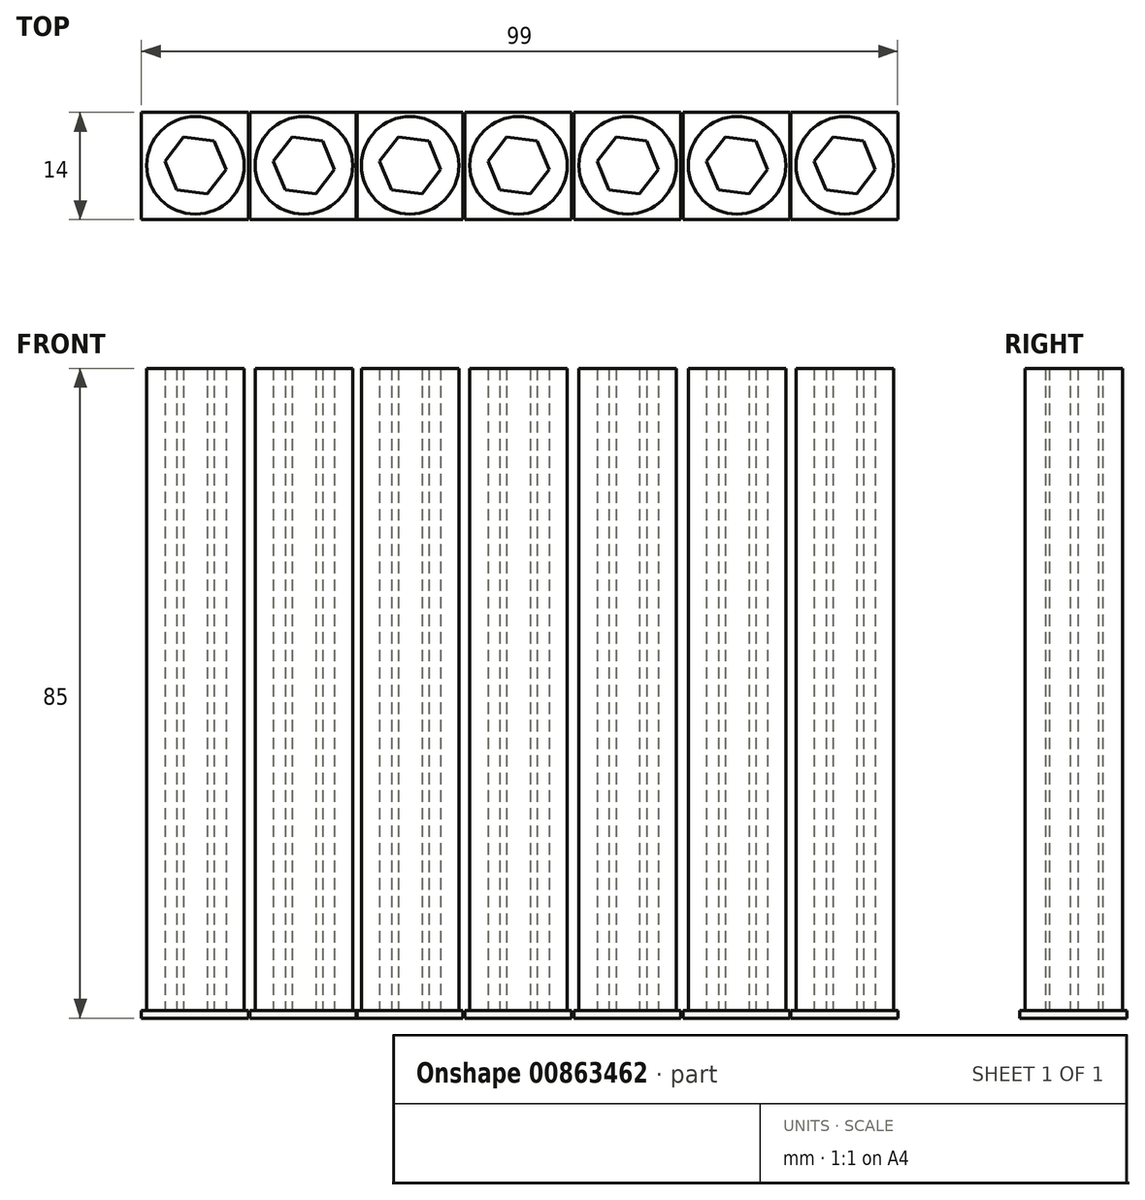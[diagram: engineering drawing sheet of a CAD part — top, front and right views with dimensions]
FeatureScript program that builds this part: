
annotation { "Feature Type Name" : "Feature", "Feature Type Description" : "" }
export const myFeature = defineFeature(function(context is Context, id is Id, definition is map)
    precondition{}
    {
        {
            var Q0;
            Q0=qCreatedBy(makeId("Top.planeOp"),FACE);
            var sketch = newSketch(context, id + "F0", { "sketchPlane" : qUnion([Q0])});
            skCircle(sketch, "E0.cCircle", {"center": v(-43.18, 23.94) * mm, "radius": 3.5 * mm, "construction": true});
            skLineSegment(sketch, "E0.0", {"start": v(-39.17, 23.42) * mm, "end": v(-41.63, 20.2) * mm});
            skLineSegment(sketch, "E0.1", {"start": v(-41.63, 20.2) * mm, "end": v(-45.63, 20.73) * mm});
            skLineSegment(sketch, "E0.2", {"start": v(-45.63, 20.73) * mm, "end": v(-47.19, 24.46) * mm});
            skLineSegment(sketch, "E0.3", {"start": v(-47.19, 24.46) * mm, "end": v(-44.73, 27.67) * mm});
            skLineSegment(sketch, "E0.4", {"start": v(-44.73, 27.67) * mm, "end": v(-40.72, 27.15) * mm});
            skLineSegment(sketch, "E0.5", {"start": v(-40.72, 27.15) * mm, "end": v(-39.17, 23.42) * mm});
            skPoint(sketch, "E0.0.midPoint", {"position": v(-40.4, 21.81) * mm});
            skCircle(sketch, "E1", {"center": v(-43.18, 23.94) * mm, "radius": 6.38 * mm});
            skSolve(sketch);
        }
        {
            var Q0;
            Q0=makeQuery(id+"F0.imprint","IMPRINT",FACE,{"disambiguationData":[TD([[makeQuery(id+"F0.imprint","IMPRINT",EDGE,{"derivedFrom":sQuery(id+"F0.wireOp",EDGE,"E0.0")}),1.0]])]});
            extrude(context, id + "F1", {"entities" : qUnion([Q0]), "depth" : 85 * mm, "offsetDistance" : 25 * mm});
        }
        {
            var Q0;
            Q0=qCreatedBy(makeId("Top.planeOp"),FACE);
            cPlane(context, id + "F2", {"entities" : qUnion([Q0]), "cplaneType" : CPlaneType.OFFSET, "offset" : 0 * mm, "oppositeDirection" : true, "width" : 150 * mm, "height" : 150 * mm});
        }
        {
            var Q0;
            Q0=qCreatedBy(id+"F2.planeOp",FACE);
            var sketch = newSketch(context, id + "F3", { "sketchPlane" : qUnion([Q0])});
            skLineSegment(sketch, "E2.bottom", {"start": v(-36.24, 30.86) * mm, "end": v(-50.24, 30.86) * mm});
            skLineSegment(sketch, "E2.top", {"start": v(-36.24, 16.86) * mm, "end": v(-50.24, 16.86) * mm});
            skLineSegment(sketch, "E2.left", {"start": v(-36.24, 30.86) * mm, "end": v(-36.24, 16.86) * mm});
            skLineSegment(sketch, "E2.right", {"start": v(-50.24, 30.86) * mm, "end": v(-50.24, 16.86) * mm});
            skPoint(sketch, "E2.middle", {"position": v(-43.24, 23.86) * mm});
            skSolve(sketch);
        }
        {
            var Q0;
            Q0 = qSketchRegion(id + "F3", true);
            extrude(context, id + "F4", {"entities" : qUnion([Q0]), "operationType" : NewBodyOperationType.ADD, "depth" : 1 * mm, "offsetDistance" : 25 * mm});
        }
        {
            var Q0;
            Q0=makeQuery(id+"F1.opExtrude","SWEPT_BODY",BODY,{"disambiguationData":[OSD([sQuery(id+"F0.wireOp",EDGE,"E0.0"),sQuery(id+"F0.wireOp",EDGE,"E0.1"),sQuery(id+"F0.wireOp",EDGE,"E0.2"),sQuery(id+"F0.wireOp",EDGE,"E0.3"),sQuery(id+"F0.wireOp",EDGE,"E0.4"),sQuery(id+"F0.wireOp",EDGE,"E0.5"),sQuery(id+"F0.wireOp",EDGE,"E1")])]});
            transform(context, id + "F5", {"entities" : qUnion([Q0]), "transformType" : TransformType.TRANSLATION_3D, "dx" : 14.2 * mm, "dy" : 0 * mm, "dz" : 0 * mm, "makeCopy" : true});
        }
        {
            var Q0;
            Q0=makeQuery(id+"F5.opPattern","COPY",BODY,{"derivedFrom":makeQuery(id+"F1.opExtrude","SWEPT_BODY",BODY,{"disambiguationData":[OSD([sQuery(id+"F0.wireOp",EDGE,"E0.0"),sQuery(id+"F0.wireOp",EDGE,"E0.1"),sQuery(id+"F0.wireOp",EDGE,"E0.2"),sQuery(id+"F0.wireOp",EDGE,"E0.3"),sQuery(id+"F0.wireOp",EDGE,"E0.4"),sQuery(id+"F0.wireOp",EDGE,"E0.5"),sQuery(id+"F0.wireOp",EDGE,"E1")])]}),"instanceName":"1"});
            transform(context, id + "F6", {"entities" : qUnion([Q0]), "transformType" : TransformType.TRANSLATION_3D, "dx" : 13.9 * mm, "dy" : 0 * mm, "dz" : 0 * mm, "makeCopy" : true});
        }
        {
            var Q0;
            Q0=makeQuery(id+"F6.opPattern","COPY",BODY,{"derivedFrom":makeQuery(id+"F5.opPattern","COPY",BODY,{"derivedFrom":makeQuery(id+"F1.opExtrude","SWEPT_BODY",BODY,{"disambiguationData":[OSD([sQuery(id+"F0.wireOp",EDGE,"E0.0"),sQuery(id+"F0.wireOp",EDGE,"E0.1"),sQuery(id+"F0.wireOp",EDGE,"E0.2"),sQuery(id+"F0.wireOp",EDGE,"E0.3"),sQuery(id+"F0.wireOp",EDGE,"E0.4"),sQuery(id+"F0.wireOp",EDGE,"E0.5"),sQuery(id+"F0.wireOp",EDGE,"E1")])]}),"instanceName":"1"}),"instanceName":"1"});
            transform(context, id + "F7", {"entities" : qUnion([Q0]), "transformType" : TransformType.TRANSLATION_3D, "dx" : 14.2 * mm, "dy" : 0 * mm, "dz" : 0 * mm, "makeCopy" : true});
        }
        {
            var Q0;
            Q0=makeQuery(id+"F7.opPattern","COPY",BODY,{"derivedFrom":makeQuery(id+"F6.opPattern","COPY",BODY,{"derivedFrom":makeQuery(id+"F5.opPattern","COPY",BODY,{"derivedFrom":makeQuery(id+"F1.opExtrude","SWEPT_BODY",BODY,{"disambiguationData":[OSD([sQuery(id+"F0.wireOp",EDGE,"E0.0"),sQuery(id+"F0.wireOp",EDGE,"E0.1"),sQuery(id+"F0.wireOp",EDGE,"E0.2"),sQuery(id+"F0.wireOp",EDGE,"E0.3"),sQuery(id+"F0.wireOp",EDGE,"E0.4"),sQuery(id+"F0.wireOp",EDGE,"E0.5"),sQuery(id+"F0.wireOp",EDGE,"E1")])]}),"instanceName":"1"}),"instanceName":"1"}),"instanceName":"1"});
            transform(context, id + "F8", {"entities" : qUnion([Q0]), "transformType" : TransformType.TRANSLATION_3D, "dx" : 14.3 * mm, "dy" : 0 * mm, "dz" : 0 * mm, "makeCopy" : true});
        }
        {
            var Q0;
            Q0=makeQuery(id+"F8.opPattern","COPY",BODY,{"derivedFrom":makeQuery(id+"F7.opPattern","COPY",BODY,{"derivedFrom":makeQuery(id+"F6.opPattern","COPY",BODY,{"derivedFrom":makeQuery(id+"F5.opPattern","COPY",BODY,{"derivedFrom":makeQuery(id+"F1.opExtrude","SWEPT_BODY",BODY,{"disambiguationData":[OSD([sQuery(id+"F0.wireOp",EDGE,"E0.0"),sQuery(id+"F0.wireOp",EDGE,"E0.1"),sQuery(id+"F0.wireOp",EDGE,"E0.2"),sQuery(id+"F0.wireOp",EDGE,"E0.3"),sQuery(id+"F0.wireOp",EDGE,"E0.4"),sQuery(id+"F0.wireOp",EDGE,"E0.5"),sQuery(id+"F0.wireOp",EDGE,"E1")])]}),"instanceName":"1"}),"instanceName":"1"}),"instanceName":"1"}),"instanceName":"1"});
            transform(context, id + "F9", {"entities" : qUnion([Q0]), "transformType" : TransformType.TRANSLATION_3D, "dx" : 14.3 * mm, "dy" : 0 * mm, "dz" : 0 * mm, "makeCopy" : true});
        }
        {
            var Q0;
            Q0=makeQuery(id+"F9.opPattern","COPY",BODY,{"derivedFrom":makeQuery(id+"F8.opPattern","COPY",BODY,{"derivedFrom":makeQuery(id+"F7.opPattern","COPY",BODY,{"derivedFrom":makeQuery(id+"F6.opPattern","COPY",BODY,{"derivedFrom":makeQuery(id+"F5.opPattern","COPY",BODY,{"derivedFrom":makeQuery(id+"F1.opExtrude","SWEPT_BODY",BODY,{"disambiguationData":[OSD([sQuery(id+"F0.wireOp",EDGE,"E0.0"),sQuery(id+"F0.wireOp",EDGE,"E0.1"),sQuery(id+"F0.wireOp",EDGE,"E0.2"),sQuery(id+"F0.wireOp",EDGE,"E0.3"),sQuery(id+"F0.wireOp",EDGE,"E0.4"),sQuery(id+"F0.wireOp",EDGE,"E0.5"),sQuery(id+"F0.wireOp",EDGE,"E1")])]}),"instanceName":"1"}),"instanceName":"1"}),"instanceName":"1"}),"instanceName":"1"}),"instanceName":"1"});
            transform(context, id + "F10", {"entities" : qUnion([Q0]), "transformType" : TransformType.TRANSLATION_3D, "dx" : 14.1 * mm, "dy" : 0 * mm, "dz" : 0 * mm, "makeCopy" : true});
        }
    });
